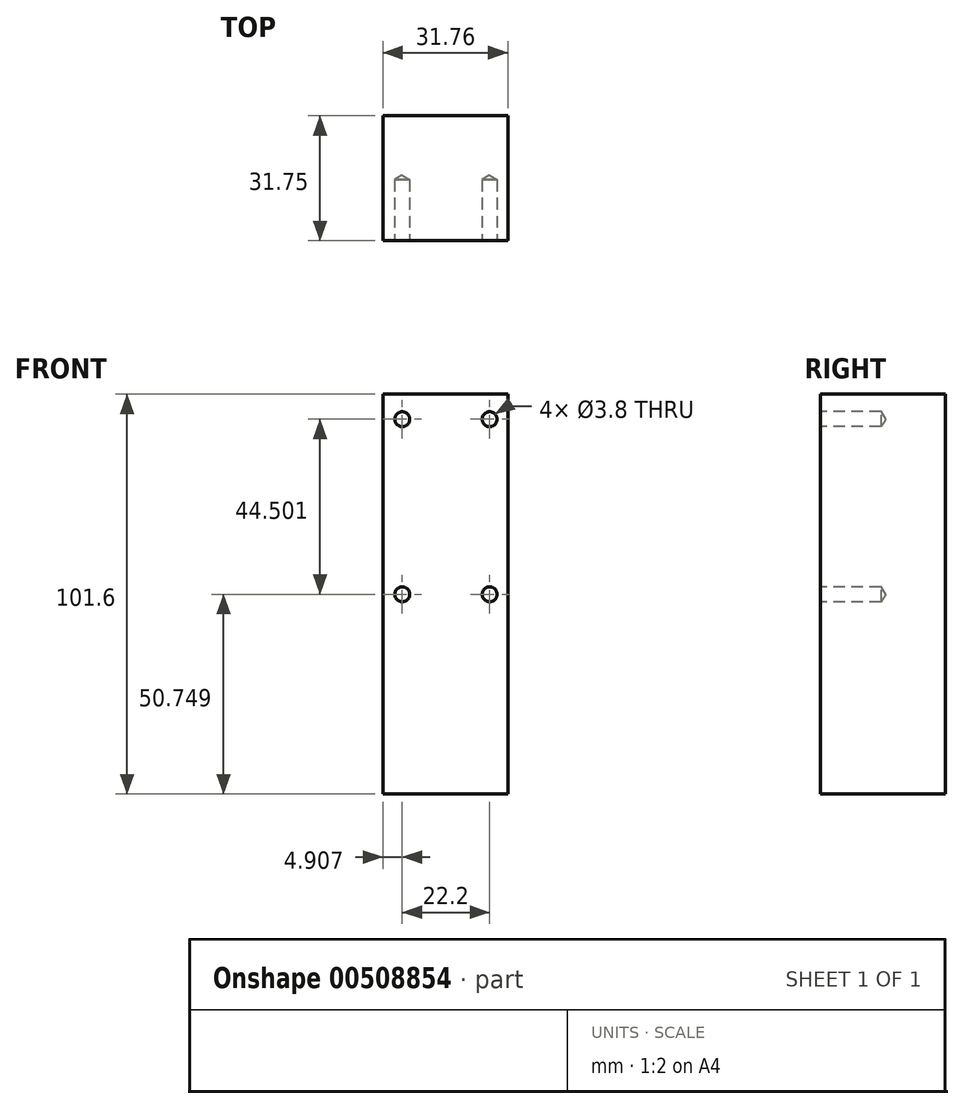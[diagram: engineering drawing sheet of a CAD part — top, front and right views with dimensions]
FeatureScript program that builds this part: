
annotation { "Feature Type Name" : "Feature", "Feature Type Description" : "" }
export const myFeature = defineFeature(function(context is Context, id is Id, definition is map)
    precondition{}
    {
        {
            var Q0;
            Q0=qCreatedBy(makeId("Front.planeOp"),FACE);
            var sketch = newSketch(context, id + "F0", { "sketchPlane" : qUnion([Q0])});
            skLineSegment(sketch, "E0.bottom", {"start": v(15.88, 50.8) * mm, "end": v(-15.88, 50.8) * mm});
            skLineSegment(sketch, "E0.top", {"start": v(15.87, -50.8) * mm, "end": v(-15.88, -50.8) * mm});
            skLineSegment(sketch, "E0.left", {"start": v(15.88, 50.8) * mm, "end": v(15.87, -50.8) * mm});
            skLineSegment(sketch, "E0.right", {"start": v(-15.88, 50.8) * mm, "end": v(-15.88, -50.8) * mm});
            skPoint(sketch, "E0.middle", {"position": v(0, 0) * mm});
            skSolve(sketch);
        }
        {
            var Q0;
            Q0=makeQuery(id+"F0.imprint","IMPRINT",FACE,{"disambiguationData":[TD([[makeQuery(id+"F0.imprint","IMPRINT",EDGE,{"derivedFrom":sQuery(id+"F0.wireOp",EDGE,"E0.bottom")}),1.0]])]});
            extrude(context, id + "F1", {"entities" : qUnion([Q0]), "depth" : 31.75 * mm});
        }
        {
            var Q0;
            Q0=makeQuery(id+"F1.opExtrude","CAP_FACE",FACE,{"disambiguationData":[OSD([sQuery(id+"F0.wireOp",EDGE,"E0.bottom"),sQuery(id+"F0.wireOp",EDGE,"E0.top"),sQuery(id+"F0.wireOp",EDGE,"E0.left"),sQuery(id+"F0.wireOp",EDGE,"E0.right")])],"isStart":false});
            var sketch = newSketch(context, id + "F2", { "sketchPlane" : qUnion([Q0])});
            skPoint(sketch, "E1", {"position": v(-10.97, 44.45) * mm});
            skPoint(sketch, "E2", {"position": v(11.23, 44.45) * mm});
            skPoint(sketch, "E3", {"position": v(-10.97, -0.05) * mm});
            skPoint(sketch, "E4", {"position": v(11.23, -0.05) * mm});
            skSolve(sketch);
        }
        {
            var Q0;
            Q0=sQuery(id+"F2.wireOp",VERTEX,"E1");
            var Q1;
            Q1=sQuery(id+"F2.wireOp",VERTEX,"E2");
            var Q2;
            Q2=sQuery(id+"F2.wireOp",VERTEX,"E3");
            var Q3;
            Q3=sQuery(id+"F2.wireOp",VERTEX,"E4");
            var Q4;
            Q4=makeQuery(id+"F1.opExtrude","SWEPT_BODY",BODY,{"disambiguationData":[OSD([sQuery(id+"F0.wireOp",EDGE,"E0.bottom"),sQuery(id+"F0.wireOp",EDGE,"E0.top"),sQuery(id+"F0.wireOp",EDGE,"E0.left"),sQuery(id+"F0.wireOp",EDGE,"E0.right")])]});
            hole(context, id + "F3", {"style" : HoleStyle.SIMPLE, "endStyle" : HoleEndStyle.BLIND, "standardTappedOrClearance" : lookupTablePath({ "standard" : "ANSI", "engagement" : "75%", "pitch" : "24 tpi", "size" : "#10", "type" : "Tapped" }), "standardBlindInLast" : lookupTablePath({ "standard" : "ANSI", "engagement" : "75%", "pitch" : "24 tpi", "size" : "#10", "type" : "Tapped" }), "holeDiameter" : 3.8 * mm, "showTappedDepth" : true, "holeDepth" : 15.5 * mm, "isTappedThrough" : true, "tappedDepth" : 12.32 * mm, "tapClearance" : 3, "locations" : qUnion([Q0, Q1, Q2, Q3]), "scope" : qUnion([Q4]), "majorDiameter" : 4.83 * mm});
        }
    });
